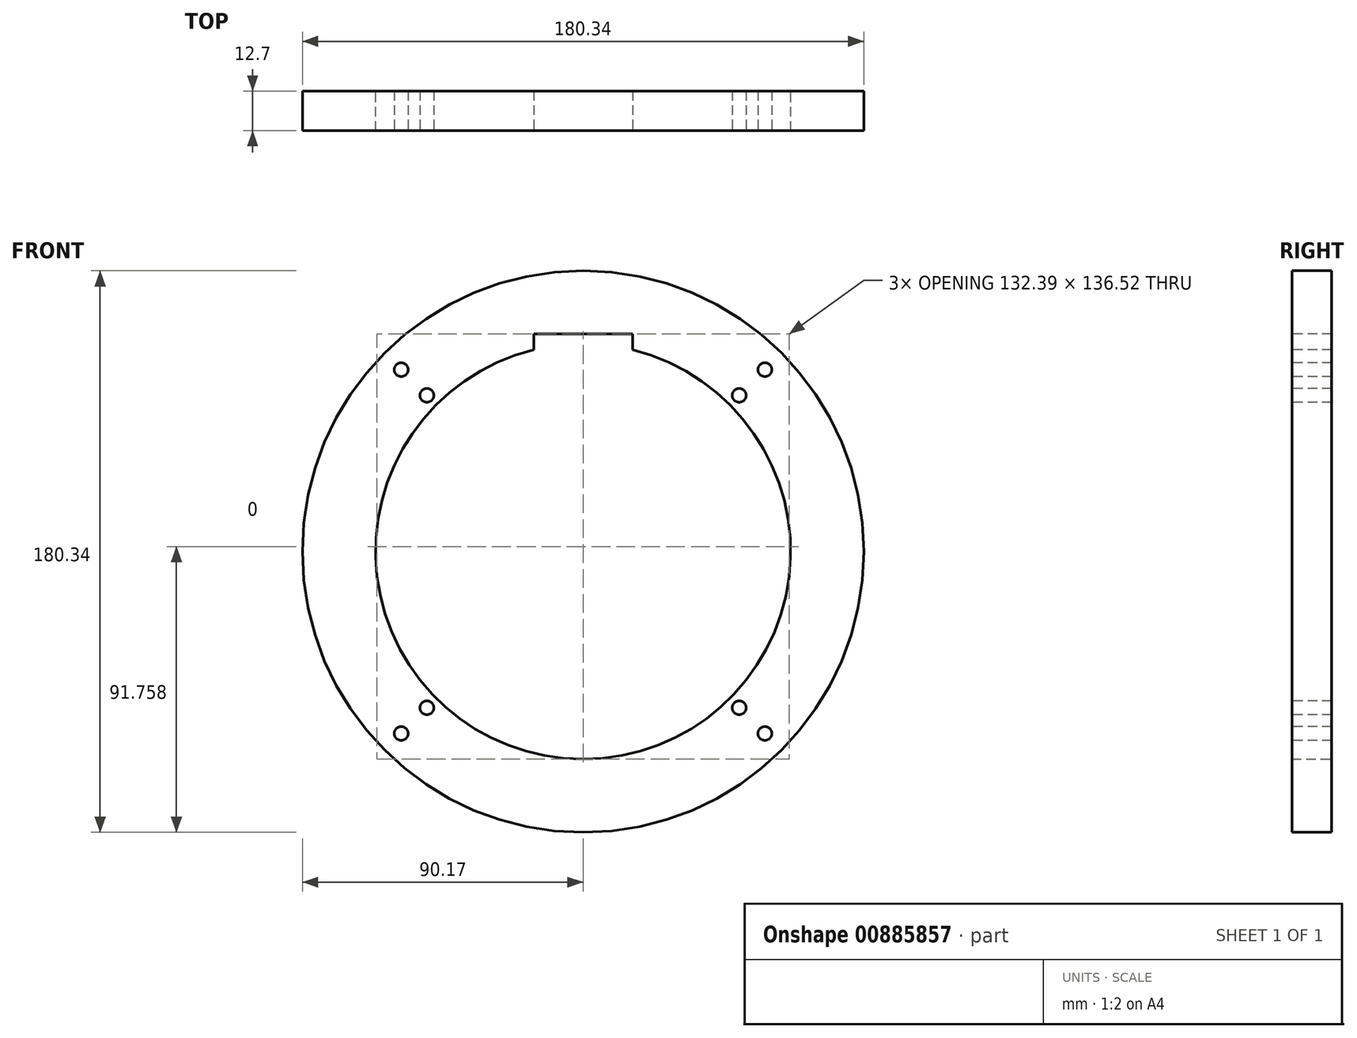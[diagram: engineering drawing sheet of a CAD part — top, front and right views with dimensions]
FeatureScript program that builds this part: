
annotation { "Feature Type Name" : "Feature", "Feature Type Description" : "" }
export const myFeature = defineFeature(function(context is Context, id is Id, definition is map)
    precondition{}
    {
        {
            var Q0;
            Q0=qCreatedBy(makeId("Front.planeOp"),FACE);
            var sketch = newSketch(context, id + "F0", { "sketchPlane" : qUnion([Q0])});
            skCircle(sketch, "E0", {"center": v(0, 0) * mm, "radius": 66.68 * mm});
            skCircle(sketch, "E1", {"center": v(0, 0) * mm, "radius": 90.17 * mm});
            skSolve(sketch);
        }
        {
            var Q0;
            Q0=makeQuery(id+"F0.imprint","IMPRINT",FACE,{"disambiguationData":[TD([[makeQuery(id+"F0.imprint","IMPRINT",EDGE,{"derivedFrom":sQuery(id+"F0.wireOp",EDGE,"E0")}),-1.0]])]});
            extrude(context, id + "F1", {"entities" : qUnion([Q0]), "depth" : 12.7 * mm, "offsetDistance" : 25.4 * mm});
        }
        {
            var Q0;
            Q0=makeQuery(id+"F1.opExtrude","CAP_FACE",FACE,{"disambiguationData":[OSD([sQuery(id+"F0.wireOp",EDGE,"E0"),sQuery(id+"F0.wireOp",EDGE,"E1")])],"isStart":false});
            var sketch = newSketch(context, id + "F2", { "sketchPlane" : qUnion([Q0])});
            skLineSegment(sketch, "E2.bottom", {"start": v(-50.17, 50.17) * mm, "end": v(50.17, 50.17) * mm, "construction": true});
            skLineSegment(sketch, "E2.top", {"start": v(-50.17, -50.17) * mm, "end": v(50.17, -50.17) * mm, "construction": true});
            skLineSegment(sketch, "E2.left", {"start": v(-50.17, 50.17) * mm, "end": v(-50.17, -50.17) * mm, "construction": true});
            skLineSegment(sketch, "E2.right", {"start": v(50.17, 50.17) * mm, "end": v(50.17, -50.17) * mm, "construction": true});
            skLineSegment(sketch, "E3", {"start": v(-50.17, 0) * mm, "end": v(50.17, 0) * mm, "construction": true});
            skLineSegment(sketch, "E4", {"start": v(0, 50.17) * mm, "end": v(0, -50.17) * mm, "construction": true});
            skLineSegment(sketch, "E5.bottom", {"start": v(-58.42, 58.42) * mm, "end": v(58.42, 58.42) * mm, "construction": true});
            skLineSegment(sketch, "E5.top", {"start": v(-58.42, -58.42) * mm, "end": v(58.42, -58.42) * mm, "construction": true});
            skLineSegment(sketch, "E5.left", {"start": v(-58.42, 58.42) * mm, "end": v(-58.42, -58.42) * mm, "construction": true});
            skLineSegment(sketch, "E5.right", {"start": v(58.42, 58.42) * mm, "end": v(58.42, -58.42) * mm, "construction": true});
            skLineSegment(sketch, "E6", {"start": v(0, 58.42) * mm, "end": v(0, -58.42) * mm, "construction": true});
            skLineSegment(sketch, "E7", {"start": v(-58.42, 0) * mm, "end": v(58.42, 0) * mm, "construction": true});
            skCircle(sketch, "E8", {"center": v(-58.42, 58.42) * mm, "radius": 2.22 * mm});
            skCircle(sketch, "E9", {"center": v(-50.17, 50.17) * mm, "radius": 2.22 * mm});
            skCircle(sketch, "E10", {"center": v(50.17, 50.17) * mm, "radius": 2.22 * mm});
            skCircle(sketch, "E11", {"center": v(58.42, 58.42) * mm, "radius": 2.22 * mm});
            skCircle(sketch, "E12", {"center": v(50.17, -50.17) * mm, "radius": 2.22 * mm});
            skCircle(sketch, "E13", {"center": v(58.42, -58.42) * mm, "radius": 2.22 * mm});
            skCircle(sketch, "E14", {"center": v(-58.42, -58.42) * mm, "radius": 2.22 * mm});
            skCircle(sketch, "E15", {"center": v(-50.17, -50.17) * mm, "radius": 2.22 * mm});
            skSolve(sketch);
        }
        {
            var Q0;
            Q0 = qSketchRegion(id + "F2", true);
            extrude(context, id + "F3", {"entities" : qUnion([Q0]), "operationType" : NewBodyOperationType.REMOVE, "endBound" : BoundingType.THROUGH_ALL, "oppositeDirection" : true, "depth" : 25.4 * mm, "offsetDistance" : 25.4 * mm});
        }
        {
            var Q0;
            Q0=makeQuery(id+"F1.opExtrude","CAP_FACE",FACE,{"disambiguationData":[OSD([sQuery(id+"F0.wireOp",EDGE,"E0"),sQuery(id+"F0.wireOp",EDGE,"E1")])],"isStart":false});
            var sketch = newSketch(context, id + "F4", { "sketchPlane" : qUnion([Q0])});
            skLineSegment(sketch, "E16.bottom", {"start": v(-15.87, 69.85) * mm, "end": v(15.87, 69.85) * mm});
            skLineSegment(sketch, "E16.top", {"start": v(-15.88, 0) * mm, "end": v(15.88, 0) * mm});
            skLineSegment(sketch, "E16.left", {"start": v(-15.87, 69.85) * mm, "end": v(-15.88, 0) * mm});
            skLineSegment(sketch, "E16.right", {"start": v(15.88, 69.85) * mm, "end": v(15.87, 0) * mm});
            skSolve(sketch);
        }
        {
            var Q0;
            {var subQ0=sQuery(id+"F4.wireOp",EDGE,"E16.bottom");Q0=makeQuery(id+"F4.imprint","IMPRINT",FACE,{"disambiguationData":[TD([[makeQuery(id+"F4.imprint","IMPRINT",EDGE,{"derivedFrom":subQ0}),-1.0]])]});}
            extrude(context, id + "F5", {"entities" : qUnion([Q0]), "operationType" : NewBodyOperationType.REMOVE, "endBound" : BoundingType.THROUGH_ALL, "oppositeDirection" : true, "depth" : 25.4 * mm, "offsetDistance" : 25.4 * mm});
        }
    });
